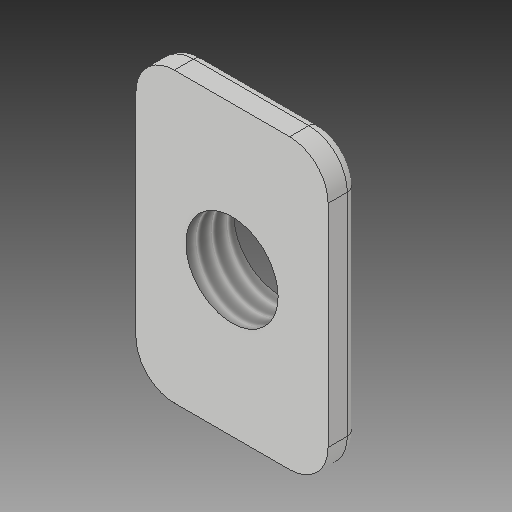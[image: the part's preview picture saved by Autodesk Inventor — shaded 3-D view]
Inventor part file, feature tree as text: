
AUTODESK INVENTOR PART (.ipt)
format: ipt  version: 2018 (Build 220112000, 112)  size: 146,432 bytes
history: native  units: mm
features: other x3, sketch x2
ambient origin geometry x8: Origin, YZ Plane, XZ Plane, XY Plane, X Axis, Y Axis, Z Axis, Center Point
bodies: Solid1 (feature_tree)
feature tree (5):
  other  "M5 Tee Nut.ipt"
  other  "Solid1::M5 Tee Nut.ipt"
  other  "TaggingFeature1"
  sketch  "Sketch1"  dims[d0=10.0mm]
  sketch  "Sketch2"
